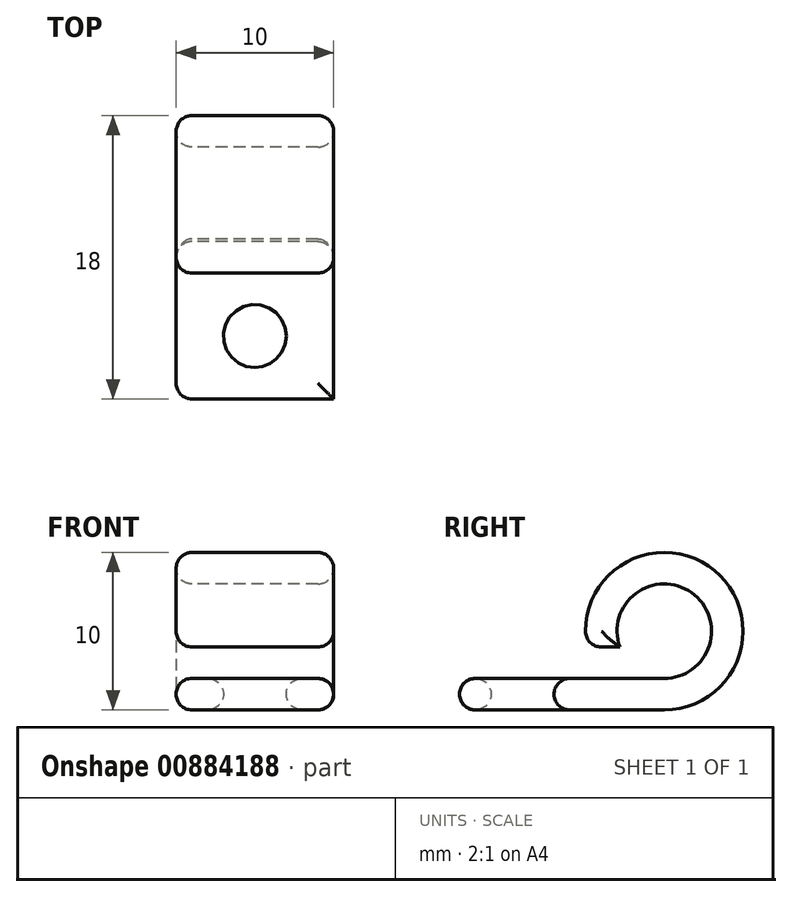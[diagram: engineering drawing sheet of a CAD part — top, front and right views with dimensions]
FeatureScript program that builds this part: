
annotation { "Feature Type Name" : "Feature", "Feature Type Description" : "" }
export const myFeature = defineFeature(function(context is Context, id is Id, definition is map)
    precondition{}
    {
        {
            var Q0;
            Q0=qCreatedBy(makeId("Top.planeOp"),FACE);
            var sketch = newSketch(context, id + "F0", { "sketchPlane" : qUnion([Q0])});
            skLineSegment(sketch, "E0.bottom", {"start": v(0, 0) * mm, "end": v(10, 0) * mm});
            skLineSegment(sketch, "E0.top", {"start": v(0, 13) * mm, "end": v(10, 13) * mm});
            skLineSegment(sketch, "E0.left", {"start": v(0, 0) * mm, "end": v(0, 13) * mm});
            skLineSegment(sketch, "E0.right", {"start": v(10, 0) * mm, "end": v(10, 13) * mm});
            skCircle(sketch, "E1", {"center": v(5, 4) * mm, "radius": 2 * mm});
            skSolve(sketch);
        }
        {
            var Q0;
            Q0=makeQuery(id+"F0.imprint","IMPRINT",FACE,{"disambiguationData":[TD([[makeQuery(id+"F0.imprint","IMPRINT",EDGE,{"derivedFrom":sQuery(id+"F0.wireOp",EDGE,"E0.bottom")}),1.0]])]});
            extrude(context, id + "F1", {"entities" : qUnion([Q0]), "depth" : 2 * mm, "offsetDistance" : 25 * mm});
        }
        {
            var Q0;
            Q0=qCreatedBy(makeId("Right.planeOp"),FACE);
            var sketch = newSketch(context, id + "F2", { "sketchPlane" : qUnion([Q0])});
            skCircle(sketch, "E2", {"center": v(13, 5) * mm, "radius": 5 * mm});
            skCircle(sketch, "E3", {"center": v(13, 5) * mm, "radius": 3 * mm});
            skLineSegment(sketch, "E4", {"start": v(8.1, 4) * mm, "end": v(10.17, 4) * mm});
            skLineSegment(sketch, "E5", {"start": v(9, 2) * mm, "end": v(13, 2) * mm});
            skSolve(sketch);
        }
        {
            var Q0;
            {var subQ0=sQuery(id+"F2.wireOp",EDGE,"E4");Q0=makeQuery(id+"F2.imprint","IMPRINT",FACE,{"disambiguationData":[TD([[makeQuery(id+"F2.imprint","IMPRINT",EDGE,{"derivedFrom":subQ0}),1.0]])]});}
            extrude(context, id + "F3", {"entities" : qUnion([Q0]), "operationType" : NewBodyOperationType.ADD, "depth" : 10 * mm, "offsetDistance" : 25 * mm});
        }
        {
            var Q0;
            Q0=makeQuery(id+"F1.opExtrude","CAP_EDGE",EDGE,{"disambiguationData":[OSD([sQuery(id+"F0.wireOp",EDGE,"E0.left")])],"isStart":false});
            var Q1;
            Q1=makeQuery(id+"F3.opExtrude","CAP_EDGE",EDGE,{"disambiguationData":[OSD([sQuery(id+"F2.wireOp",EDGE,"E3")])],"isStart":true});
            var Q2;
            Q2=makeQuery(id+"F3.boolean.opBoolean","MERGE",FACE,{"derivedFrom":[makeQuery(id+"F1.opExtrude","SWEPT_FACE",FACE,{"disambiguationData":[OSD([sQuery(id+"F0.wireOp",EDGE,"E0.left")])]}),makeQuery(id+"F3.opExtrude","CAP_FACE",FACE,{"disambiguationData":[OSD([sQuery(id+"F2.wireOp",EDGE,"E2"),sQuery(id+"F2.wireOp",EDGE,"E3"),sQuery(id+"F2.wireOp",EDGE,"E4"),sQuery(id+"F2.wireOp",EDGE,"E5")])],"isStart":true})]});
            var Q3;
            Q3=makeQuery(id+"F3.opExtrude","CAP_EDGE",EDGE,{"disambiguationData":[OSD([sQuery(id+"F2.wireOp",EDGE,"E3")])],"isStart":false});
            var Q4;
            Q4=makeQuery(id+"F3.opExtrude","CAP_EDGE",EDGE,{"disambiguationData":[OSD([sQuery(id+"F2.wireOp",EDGE,"E2")])],"isStart":false});
            var Q5;
            Q5=makeQuery(id+"F1.opExtrude","CAP_EDGE",EDGE,{"disambiguationData":[OSD([sQuery(id+"F0.wireOp",EDGE,"E0.right")])],"isStart":false});
            var Q6;
            Q6=makeQuery(id+"F1.opExtrude","CAP_EDGE",EDGE,{"disambiguationData":[OSD([sQuery(id+"F0.wireOp",EDGE,"E0.right")])],"isStart":true});
            var Q7;
            Q7=makeQuery(id+"F3.opExtrude","SWEPT_EDGE",EDGE,{"disambiguationData":[OSD([sQuery(id+"F2.wireOp",EDGE,"E2"),sQuery(id+"F2.wireOp",EDGE,"E4")])]});
            var Q8;
            Q8=makeQuery(id+"F3.opExtrude","CAP_EDGE",EDGE,{"disambiguationData":[OSD([sQuery(id+"F2.wireOp",EDGE,"E4")])],"isStart":true});
            var Q9;
            Q9=makeQuery(id+"F3.opExtrude","CAP_EDGE",EDGE,{"disambiguationData":[OSD([sQuery(id+"F2.wireOp",EDGE,"E4")])],"isStart":false});
            var Q10;
            Q10=makeQuery(id+"F1.opExtrude","CAP_EDGE",EDGE,{"disambiguationData":[OSD([sQuery(id+"F0.wireOp",EDGE,"E0.bottom")])],"isStart":false});
            var Q11;
            Q11=makeQuery(id+"F1.opExtrude","CAP_EDGE",EDGE,{"disambiguationData":[OSD([sQuery(id+"F0.wireOp",EDGE,"E0.bottom")])],"isStart":true});
            var Q12;
            Q12=makeQuery(id+"F1.opExtrude","CAP_EDGE",EDGE,{"disambiguationData":[OSD([sQuery(id+"F0.wireOp",EDGE,"E1")])],"isStart":false});
            var Q13;
            Q13=makeQuery(id+"F1.opExtrude","CAP_EDGE",EDGE,{"disambiguationData":[OSD([sQuery(id+"F0.wireOp",EDGE,"E1")])],"isStart":true});
            fillet(context, id + "F4", {"entities" : qUnion([Q0, Q1, Q2, Q3, Q4, Q5, Q6, Q7, Q8, Q9, Q10, Q11, Q12, Q13]), "radius" : 1 * mm, "tangentPropagation" : true, "allowEdgeOverflow" : false});
        }
    });
